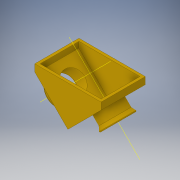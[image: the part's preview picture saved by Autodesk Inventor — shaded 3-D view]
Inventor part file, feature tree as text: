
AUTODESK INVENTOR PART (.ipt)
format: ipt  version: 2017 (Build 210142000, 142)  size: 225,792 bytes
history: native  units: in
note: dims shown in document units (in); Inventor stores cm internally (conversion verified against a paired STEP export)
features: extrude x7, sketch x5, fillet x4, other x2, chamfer x2, shell x1
ambient origin geometry x8: Origin, YZ Plane, XZ Plane, XY Plane, X Axis, Y Axis, Z Axis, Center Point
bodies: Solid1 (feature_tree)
feature tree (21):
  extrude  "Extrusion1"  Depth=1.9685in TaperAngle=0.0deg
  shell  "Shell2"  Thickness=1.0236in
  sketch  "Sketch2"  dims[d6=0.9843in d7=1.1811in]
  sketch  "Sketch3"  dims[d8=1.0236in d9=1.1811in]
  extrude  "Extrusion2"  Depth=1.1811in
  extrude  "Extrusion3"  Depth=1.1811in
  extrude  "Extrusion6"  Depth=0.3937in TaperAngle=0.0deg
  extrude  "Extrusion7"  Depth=0.0197in
  other  "Work Axis1"
  other  "Work Axis2"
  extrude  "Extrusion12"  Depth=0.5906in TaperAngle=0.0deg
  chamfer  "Chamfer2"  Distance=1.1811in
  fillet  "Fillet3"  Radius=0.5906in
  fillet  "Fillet4"  Radius=2.9528in
  extrude  "Extrusion19"  Depth=1.9685in
  chamfer  "Chamfer3"  Distance=0.1969in
  fillet  "Fillet7"  Radius=0.1181in
  fillet  "Fillet8"  Radius=1.3386in
  sketch  "Sketch1"  dims[d0=45.0deg d3=1.9685in d4=0.0in d5=1.0236in]
  sketch  "Sketch9"  dims[d10=0.9843in d12=0.3937in d13=0.0in]
  sketch  "Sketch16"  dims[d14=0.3937in d15=0.0in d26=1.1811in d27=0.5906in d28=0.0in d29=1.1811in d30=0.5906in d31=0.0in d39=2.9528in d41=1.9685in d42=0.1969in d43=0.1181in d81=1.3386in d82=0.1969in d83=0.0in d84=0.1575in d85=0.0787in d86=0.1718in d87=0.1181in d88=0.0197in d134=1.3386in d135=0.1969in d136=0.0in d138=0.0787in d139=0.1575in d140=0.1718in d141=0.1181in d142=0.0197in d93=0.0394in d94=0.0394in]
